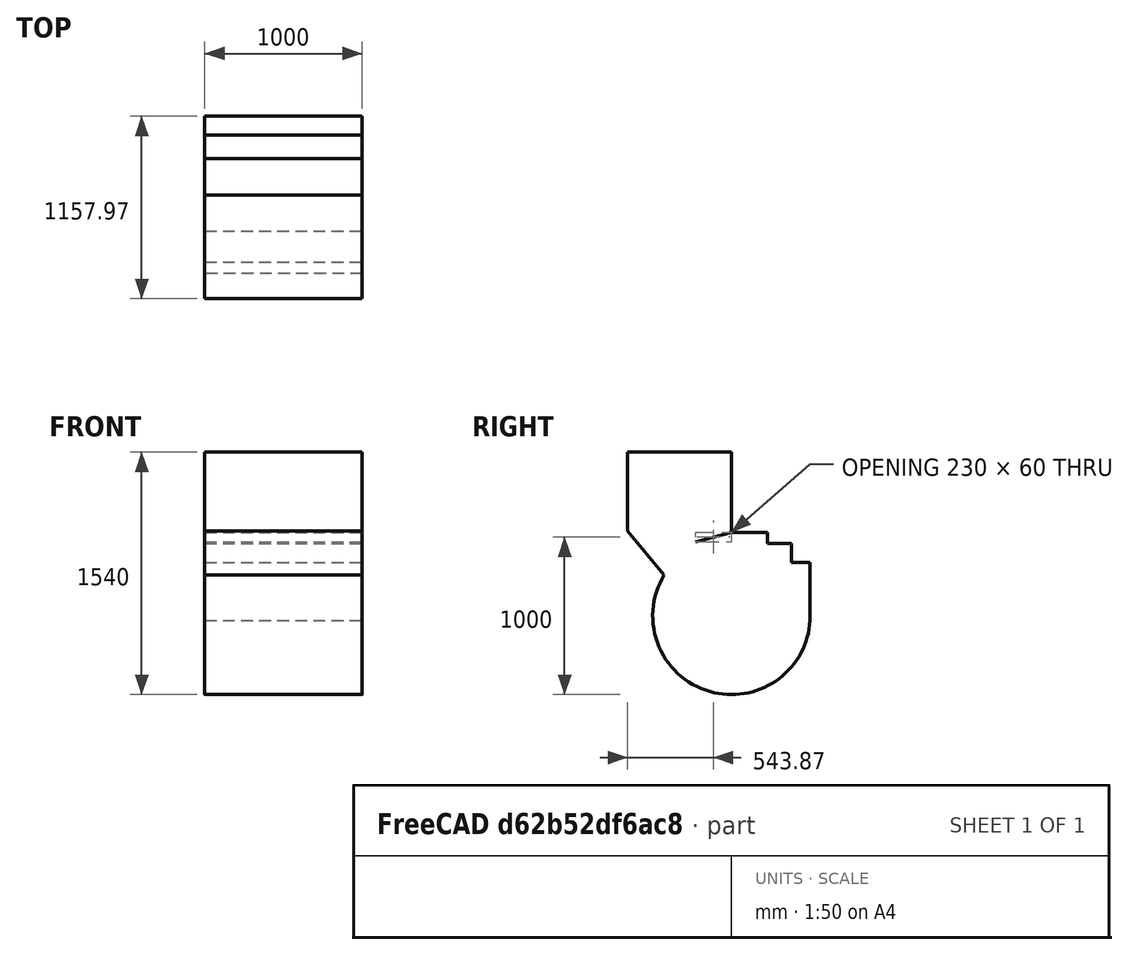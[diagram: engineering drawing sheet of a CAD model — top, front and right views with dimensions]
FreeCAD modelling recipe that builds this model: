
FCSTD DOCUMENT
Label: Shell_no_bin
objects: Sketcher::SketchObject×1, PartDesign::Pad×1
note: 3 computed .brp shape members not serialized (recipe doc carries the construction recipe); baked Part::Feature solids carry a one-line shape summary decoded from their .brp

FEATURE [Sketcher::SketchObject] Sketch  label="Shell "
  Placement = pos=(-500,0,0) rot=(0.57735,0.57735,0.57735;2.0944rad)
  sketch-geometry (13):
    g0: ArcOfCircle CenterX=0 CenterY=0 CenterZ=0 NormalX=0 NormalY=0 NormalZ=1 Radius=500 StartAngle=2.59474 EndAngle=4.49535
    g1: LineSegment StartX=-427.083 StartY=260 StartZ=0 EndX=-658.874 EndY=540 EndZ=0
    g2: LineSegment StartX=0 StartY=530 StartZ=0 EndX=230 EndY=530 EndZ=0
    g3: LineSegment StartX=230 StartY=530 StartZ=0 EndX=230 EndY=460 EndZ=0
    g4: LineSegment StartX=230 StartY=460 StartZ=0 EndX=380 EndY=460 EndZ=0
    g5: LineSegment StartX=380 StartY=460 StartZ=0 EndX=380 EndY=340 EndZ=0
    g6: LineSegment StartX=380 StartY=340 StartZ=0 EndX=499.099 EndY=340 EndZ=0
    g7: LineSegment StartX=499.099 StartY=340 StartZ=0 EndX=499.099 EndY=-30 EndZ=0
    g8: LineSegment StartX=-658.874 StartY=1040 StartZ=0 EndX=-658.874 EndY=540 EndZ=0
    g9: LineSegment StartX=0 StartY=530 StartZ=0 EndX=-230 EndY=470 EndZ=0
    g10: ArcOfCircle CenterX=0 CenterY=0 CenterZ=0 NormalX=0 NormalY=0 NormalZ=1 Radius=500 StartAngle=4.49535 EndAngle=6.22315
    g11: LineSegment StartX=-658.874 StartY=1040 StartZ=0 EndX=0 EndY=1040 EndZ=0
    g12: LineSegment StartX=0 StartY=1040 StartZ=0 EndX=0 EndY=530 EndZ=0
  constraints (40):
    c: Radius(g0) = 500
    c: DistanceX(g0) = 0
    c: DistanceY(g0) = 0
    c: Horizontal(g2)
    c: Vertical(g3)
    c: Coincident(g4,g3)
    c: Horizontal(g4)
    c: Vertical(g5)
    c: Coincident(g6,g5)
    c: Horizontal(g6)
    c: DistanceY(g1) = 540
    c: Coincident(g2,g3)
    c: Coincident(g4,g5)
    c: Coincident(g7,g10)
    c: Vertical(g7)
    c: Distance(g7) = 370
    c: Coincident(g1,g0)
    c: Coincident(g8,g1)
    c: Vertical(g8)
    c: Distance(g1) = 363.493
    c: Distance(g8) = 500
    c: Coincident(g0,g10)
    c: Coincident(g11,g8)
    c: Horizontal(g11)
    c: Coincident(g12,g11)
    c: Vertical(g12)
    c: Coincident(g6,g7)
    c: Coincident(g9,g2)
    c: Coincident(g12,g2)
    c: DistanceX(g5) = 380
    c: DistanceY(g5) = 340
    c: DistanceX(g3) = 230
    c: DistanceY(g3) = 460
    c: DistanceX(g2) = 0
    c: DistanceY(g2) = 530
    c: DistanceX(g9) = -230
    c: DistanceY(g9) = 470
    c: DistanceY(g0) = 260
    c: Coincident(g10,g0)
    c: DistanceY(g0) = -488.27
FEATURE [PartDesign::Pad] Pad  label="Shell_"
  Length = 1000
  MirroredExtent = false
  Sketch = -> Sketch
